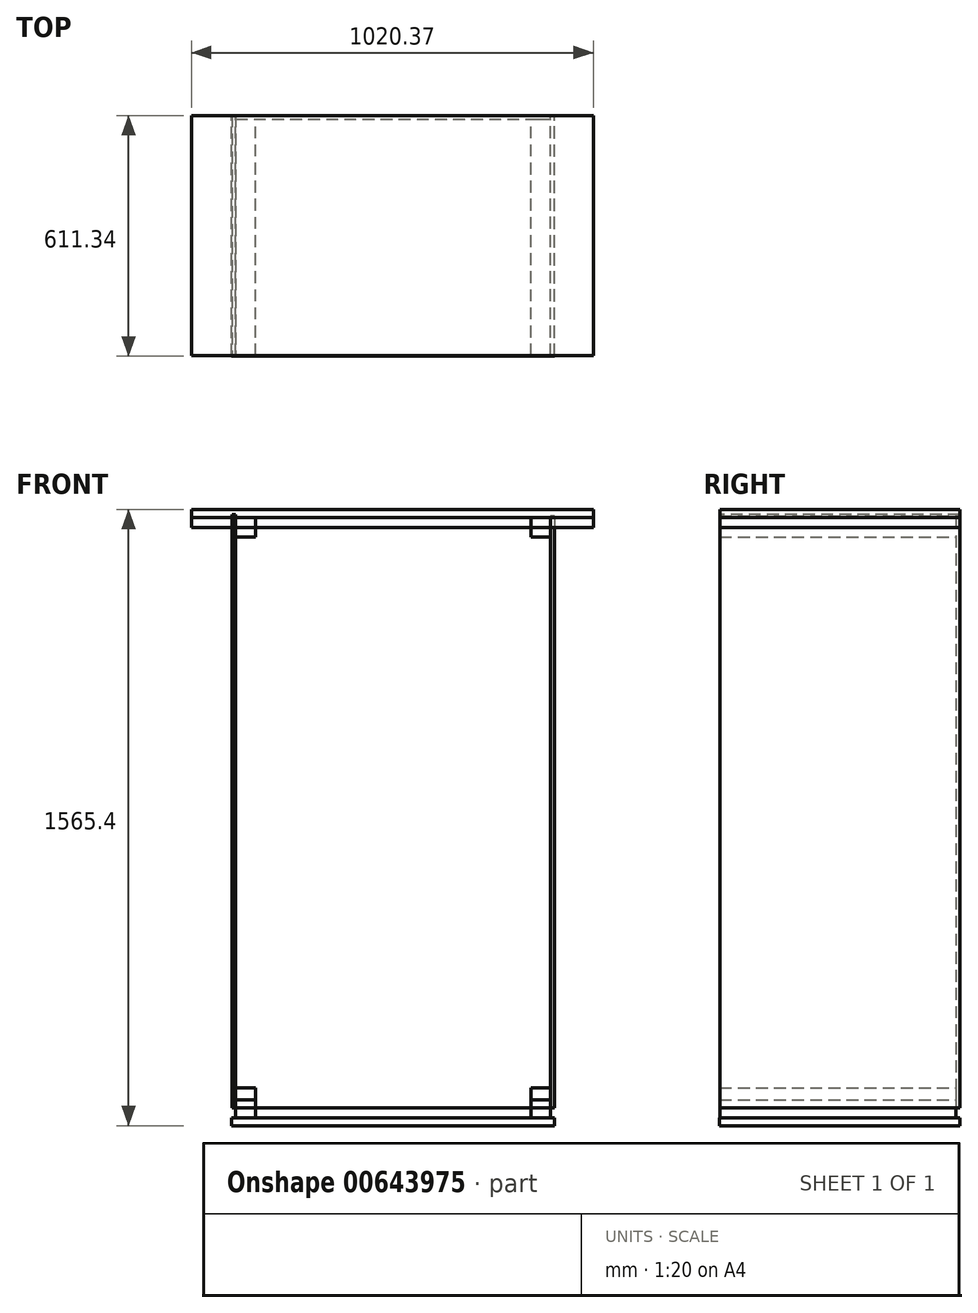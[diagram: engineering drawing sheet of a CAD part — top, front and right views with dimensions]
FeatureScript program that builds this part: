
annotation { "Feature Type Name" : "Feature", "Feature Type Description" : "" }
export const myFeature = defineFeature(function(context is Context, id is Id, definition is map)
    precondition{}
    {
        {
            var Q0;
            Q0=qCreatedBy(makeId("Front.planeOp"),FACE);
            var sketch = newSketch(context, id + "F0", { "sketchPlane" : qUnion([Q0])});
            skLineSegment(sketch, "E0.bottom", {"start": v(-1495.03, 1500) * mm, "end": v(-695.03, 1500) * mm});
            skLineSegment(sketch, "E0.top", {"start": v(-1495.03, 0) * mm, "end": v(-695.03, 0) * mm});
            skLineSegment(sketch, "E0.left", {"start": v(-1495.03, 1500) * mm, "end": v(-1495.03, 0) * mm});
            skLineSegment(sketch, "E0.right", {"start": v(-695.03, 1500) * mm, "end": v(-695.03, 0) * mm});
            skSolve(sketch);
        }
        {
            var Q0;
            Q0=makeQuery(id+"F0.imprint","IMPRINT",FACE,{"disambiguationData":[TD([[makeQuery(id+"F0.imprint","IMPRINT",EDGE,{"derivedFrom":sQuery(id+"F0.wireOp",EDGE,"E0.bottom")}),-1.0]])]});
            extrude(context, id + "F1", {"entities" : qUnion([Q0]), "depth" : 10 * mm, "offsetDistance" : 25.4 * mm});
        }
        {
            var Q0;
            Q0=makeQuery(id+"F1.opExtrude","CAP_FACE",FACE,{"disambiguationData":[OSD([sQuery(id+"F0.wireOp",EDGE,"E0.bottom"),sQuery(id+"F0.wireOp",EDGE,"E0.top"),sQuery(id+"F0.wireOp",EDGE,"E0.left"),sQuery(id+"F0.wireOp",EDGE,"E0.right")])],"isStart":false});
            var sketch = newSketch(context, id + "F2", { "sketchPlane" : qUnion([Q0])});
            skLineSegment(sketch, "E1", {"start": v(-1095.03, 1500) * mm, "end": v(-1095.03, 0) * mm});
            skLineSegment(sketch, "E2", {"start": v(-1495.03, 750) * mm, "end": v(-695.03, 750) * mm});
            skLineSegment(sketch, "E3.bottom", {"start": v(-1495.03, 1500) * mm, "end": v(-1445.03, 1500) * mm});
            skLineSegment(sketch, "E3.top", {"start": v(-1495.03, 1450) * mm, "end": v(-1445.03, 1450) * mm});
            skLineSegment(sketch, "E3.left", {"start": v(-1495.03, 1500) * mm, "end": v(-1495.03, 1450) * mm});
            skLineSegment(sketch, "E3.right", {"start": v(-1445.03, 1500) * mm, "end": v(-1445.03, 1450) * mm});
            skLineSegment(sketch, "E4.MirrorCS", {"start": v(-745.03, 1500) * mm, "end": v(-745.03, 1450) * mm});
            skLineSegment(sketch, "E5.MirrorCS", {"start": v(-695.03, 1450) * mm, "end": v(-745.03, 1450) * mm});
            skLineSegment(sketch, "E6.MirrorCS", {"start": v(-695.03, 1500) * mm, "end": v(-695.03, 1450) * mm});
            skLineSegment(sketch, "E7.MirrorCS", {"start": v(-695.03, 1500) * mm, "end": v(-745.03, 1500) * mm});
            skLineSegment(sketch, "E8.MirrorCS", {"start": v(-695.03, 50) * mm, "end": v(-745.03, 50) * mm});
            skLineSegment(sketch, "E9.MirrorCS", {"start": v(-745.03, 0) * mm, "end": v(-745.03, 50) * mm});
            skLineSegment(sketch, "E10.MirrorCS", {"start": v(-695.03, 0) * mm, "end": v(-745.03, 0) * mm});
            skLineSegment(sketch, "E11.MirrorCS", {"start": v(-695.03, 0) * mm, "end": v(-695.03, 50) * mm});
            skLineSegment(sketch, "E12.MirrorCS", {"start": v(-1495.03, 50) * mm, "end": v(-1445.03, 50) * mm});
            skLineSegment(sketch, "E13.MirrorCS", {"start": v(-1445.03, 0) * mm, "end": v(-1445.03, 50) * mm});
            skLineSegment(sketch, "E14.MirrorCS", {"start": v(-1495.03, 0) * mm, "end": v(-1495.03, 50) * mm});
            skLineSegment(sketch, "E15.MirrorCS", {"start": v(-1495.03, 0) * mm, "end": v(-1445.03, 0) * mm});
            skSolve(sketch);
        }
        {
            var Q0;
            Q0=makeQuery(id+"F2.imprint","IMPRINT",FACE,{"disambiguationData":[TD([[makeQuery(id+"F2.imprint","IMPRINT",EDGE,{"derivedFrom":sQuery(id+"F2.wireOp",EDGE,"E3.bottom")}),-1.0]])]});
            var Q1;
            Q1=makeQuery(id+"F2.imprint","IMPRINT",FACE,{"disambiguationData":[TD([[makeQuery(id+"F2.imprint","IMPRINT",EDGE,{"derivedFrom":sQuery(id+"F2.wireOp",EDGE,"E5.MirrorCS")}),-1.0]])]});
            var Q2;
            Q2=makeQuery(id+"F2.imprint","IMPRINT",FACE,{"disambiguationData":[TD([[makeQuery(id+"F2.imprint","IMPRINT",EDGE,{"derivedFrom":sQuery(id+"F2.wireOp",EDGE,"E12.MirrorCS")}),-1.0]])]});
            var Q3;
            Q3=makeQuery(id+"F2.imprint","IMPRINT",FACE,{"disambiguationData":[TD([[makeQuery(id+"F2.imprint","IMPRINT",EDGE,{"derivedFrom":sQuery(id+"F2.wireOp",EDGE,"E8.MirrorCS")}),1.0]])]});
            extrude(context, id + "F3", {"entities" : qUnion([Q0, Q1, Q2, Q3]), "depth" : 600 * mm, "offsetDistance" : 25.4 * mm});
        }
        {
            var Q0;
            Q0=makeQuery(id+"F3.opExtrude","SWEPT_FACE",FACE,{"disambiguationData":[OSD([sQuery(id+"F2.wireOp",EDGE,"E11.MirrorCS")])]});
            var sketch = newSketch(context, id + "F4", { "sketchPlane" : qUnion([Q0])});
            skLineSegment(sketch, "E16.bottom", {"start": v(-609.72, 1503.91) * mm, "end": v(0, 1503.91) * mm});
            skLineSegment(sketch, "E16.top", {"start": v(-609.72, 0) * mm, "end": v(0, 0) * mm});
            skLineSegment(sketch, "E16.left", {"start": v(-609.72, 1503.91) * mm, "end": v(-609.72, 0) * mm});
            skLineSegment(sketch, "E16.right", {"start": v(0, 1503.91) * mm, "end": v(0, 0) * mm});
            skSolve(sketch);
        }
        {
            var Q0;
            {var subQ1=sQuery(id+"F4.wireOp",EDGE,"E16.bottom");Q0=makeQuery(id+"F4.imprint","IMPRINT",FACE,{"disambiguationData":[TD([[makeQuery(id+"F4.imprint","IMPRINT",EDGE,{"derivedFrom":subQ1}),-1.0]])]});}
            var Q1;
            {var subQ1=sQuery(id+"F2.wireOp",EDGE,"E11.MirrorCS");var subQ2=makeQuery(id+"F3.opExtrude","CAP_EDGE",EDGE,{"disambiguationData":[OSD([subQ1])],"isStart":true});Q1=makeQuery(id+"F4.imprint","IMPRINT",FACE,{"disambiguationData":[TD([[makeQuery(id+"F4.imprint","IMPRINT",EDGE,{"derivedFrom":subQ2}),-1.0]])]});}
            extrude(context, id + "F5", {"entities" : qUnion([Q0, Q1]), "depth" : 10 * mm, "offsetDistance" : 25.4 * mm});
        }
        {
            var Q0;
            Q0=makeQuery(id+"F3.opExtrude","SWEPT_FACE",FACE,{"disambiguationData":[OSD([sQuery(id+"F2.wireOp",EDGE,"E14.MirrorCS")])]});
            var sketch = newSketch(context, id + "F6", { "sketchPlane" : qUnion([Q0])});
            skLineSegment(sketch, "E17.bottom", {"start": v(0, 1507.84) * mm, "end": v(610, 1507.84) * mm});
            skLineSegment(sketch, "E17.top", {"start": v(0, 0) * mm, "end": v(610, 0) * mm});
            skLineSegment(sketch, "E17.left", {"start": v(0, 1507.84) * mm, "end": v(0, 0) * mm});
            skLineSegment(sketch, "E17.right", {"start": v(610, 1507.84) * mm, "end": v(610, 0) * mm});
            skSolve(sketch);
        }
        {
            var Q0;
            {var subQ3=sQuery(id+"F6.wireOp",EDGE,"E17.bottom");Q0=makeQuery(id+"F6.imprint","IMPRINT",FACE,{"disambiguationData":[TD([[makeQuery(id+"F6.imprint","IMPRINT",EDGE,{"derivedFrom":subQ3}),-1.0]])]});}
            var Q1;
            {var subQ1=sQuery(id+"F2.wireOp",EDGE,"E14.MirrorCS");var subQ2=makeQuery(id+"F3.opExtrude","CAP_EDGE",EDGE,{"disambiguationData":[OSD([subQ1])],"isStart":true});Q1=makeQuery(id+"F6.imprint","IMPRINT",FACE,{"disambiguationData":[TD([[makeQuery(id+"F6.imprint","IMPRINT",EDGE,{"derivedFrom":subQ2}),1.0]])]});}
            extrude(context, id + "F7", {"entities" : qUnion([Q0, Q1]), "depth" : 10 * mm, "offsetDistance" : 25.4 * mm});
        }
        {
            var Q0;
            Q0=makeQuery(id+"F3.opExtrude","SWEPT_FACE",FACE,{"disambiguationData":[OSD([sQuery(id+"F2.wireOp",EDGE,"E3.bottom")])]});
            var sketch = newSketch(context, id + "F8", { "sketchPlane" : qUnion([Q0])});
            skPoint(sketch, "E18.left.start.orphan", {"position": v(-1495.03, 0) * mm});
            skLineSegment(sketch, "E19.bottom", {"start": v(-1607.3, -610) * mm, "end": v(-586.93, -610) * mm});
            skLineSegment(sketch, "E19.top", {"start": v(-1607.3, 0) * mm, "end": v(-586.93, 0) * mm});
            skLineSegment(sketch, "E19.left", {"start": v(-1607.3, -610) * mm, "end": v(-1607.3, 0) * mm});
            skLineSegment(sketch, "E19.right", {"start": v(-586.93, -610) * mm, "end": v(-586.93, 0) * mm});
            skSolve(sketch);
        }
        {
            var Q0;
            Q0 = qSketchRegion(id + "F8", true);
            extrude(context, id + "F9", {"entities" : qUnion([Q0]), "depth" : 20 * mm, "offsetDistance" : 25.4 * mm});
        }
        {
            var Q0;
            Q0 = qSketchRegion(id + "F8", true);
            var Q1;
            Q1=makeQuery(id+"F9.opExtrude","CAP_FACE",FACE,{"disambiguationData":[OSD([sQuery(id+"F8.wireOp",EDGE,"E19.bottom"),sQuery(id+"F8.wireOp",EDGE,"E19.top"),sQuery(id+"F8.wireOp",EDGE,"E19.left"),sQuery(id+"F8.wireOp",EDGE,"E19.right")])],"isStart":true});
            var Q2;
            Q2=makeQuery(id+"F3.opExtrude","SWEPT_FACE",FACE,{"disambiguationData":[OSD([sQuery(id+"F2.wireOp",EDGE,"E10.MirrorCS")])]});
            var Q3;
            Q3=makeQuery(id+"F3.opExtrude","SWEPT_FACE",FACE,{"disambiguationData":[OSD([sQuery(id+"F2.wireOp",EDGE,"E15.MirrorCS")])]});
            extrude(context, id + "F10", {"entities" : qUnion([Q0, Q1, Q2, Q3]), "depth" : 20 * mm, "offsetDistance" : 25.4 * mm});
        }
        {
            var Q0;
            Q0=makeQuery(id+"F3.opExtrude","SWEPT_FACE",FACE,{"disambiguationData":[OSD([sQuery(id+"F2.wireOp",EDGE,"E10.MirrorCS")])]});
            var Q1;
            Q1=makeQuery(id+"F9.opExtrude","CAP_FACE",FACE,{"disambiguationData":[OSD([sQuery(id+"F8.wireOp",EDGE,"E19.bottom"),sQuery(id+"F8.wireOp",EDGE,"E19.top"),sQuery(id+"F8.wireOp",EDGE,"E19.left"),sQuery(id+"F8.wireOp",EDGE,"E19.right")])],"isStart":true});
            var Q2;
            Q2=makeQuery(id+"F3.opExtrude","SWEPT_FACE",FACE,{"disambiguationData":[OSD([sQuery(id+"F2.wireOp",EDGE,"E15.MirrorCS")])]});
            extrude(context, id + "F11", {"entities" : qUnion([Q0, Q1, Q2]), "depth" : 25.4 * mm, "offsetDistance" : 25.4 * mm});
        }
        {
            var Q0;
            Q0=makeQuery(id+"F11.opExtrude","CAP_FACE",FACE,{"disambiguationData":[OSD([sQuery(id+"F2.wireOp",EDGE,"E15.MirrorCS")])],"isStart":false});
            var sketch = newSketch(context, id + "F12", { "sketchPlane" : qUnion([Q0])});
            skLineSegment(sketch, "E20.bottom", {"start": v(-685.2, 611.34) * mm, "end": v(-1505.83, 611.34) * mm});
            skLineSegment(sketch, "E20.top", {"start": v(-685.2, 0) * mm, "end": v(-1505.83, 0) * mm});
            skLineSegment(sketch, "E20.left", {"start": v(-685.2, 611.34) * mm, "end": v(-685.2, 0) * mm});
            skLineSegment(sketch, "E20.right", {"start": v(-1505.83, 611.34) * mm, "end": v(-1505.83, 0) * mm});
            skSolve(sketch);
        }
        {
            var Q0;
            Q0=makeQuery(id+"F12.imprint","IMPRINT",FACE,{"disambiguationData":[TD([[makeQuery(id+"F12.imprint","IMPRINT",EDGE,{"derivedFrom":sQuery(id+"F12.wireOp",EDGE,"E20.bottom")}),1.0]])]});
            var Q1;
            {var subQ0=sQuery(id+"F2.wireOp",EDGE,"E15.MirrorCS");Q1=makeQuery(id+"F12.imprint","IMPRINT",FACE,{"disambiguationData":[TD([[makeQuery(id+"F12.imprint","IMPRINT",EDGE,{"derivedFrom":makeQuery(id+"F11.opExtrude","CAP_EDGE",EDGE,{"disambiguationData":[OSD([subQ0]),TDD([makeQuery(id+"F3.opExtrude","CAP_EDGE",EDGE,{"disambiguationData":[OSD([subQ0])],"isStart":true})])],"isStart":false})}),1.0]])]});}
            extrude(context, id + "F13", {"entities" : qUnion([Q0, Q1]), "depth" : 20 * mm, "offsetDistance" : 25.4 * mm});
        }
    });
